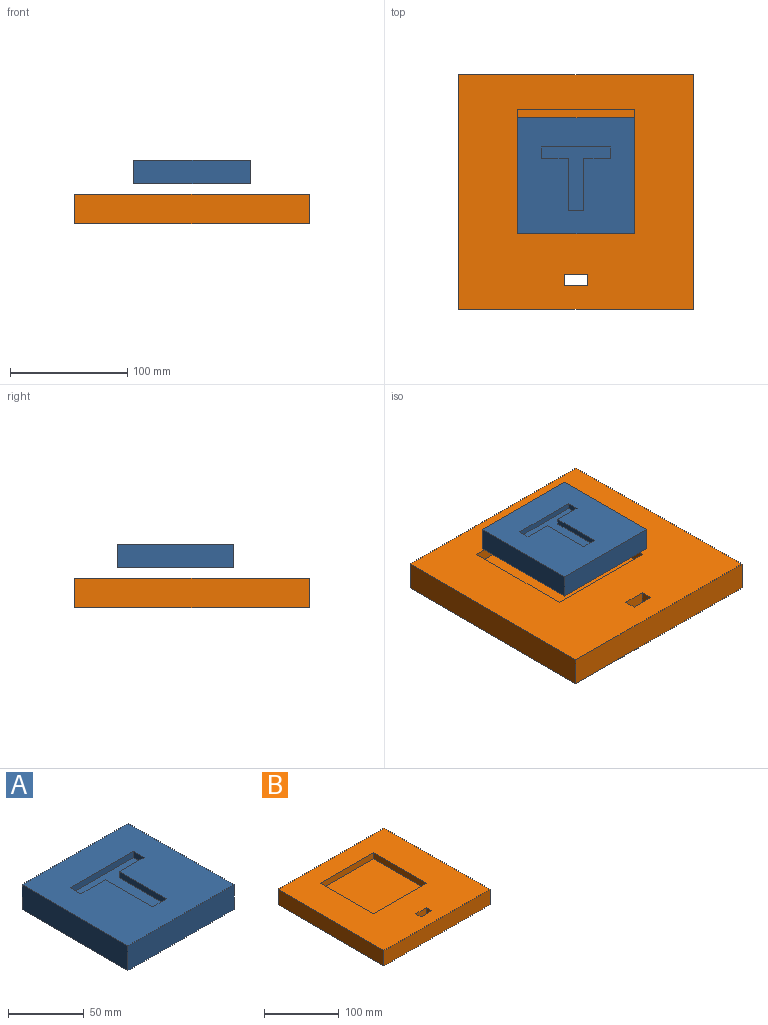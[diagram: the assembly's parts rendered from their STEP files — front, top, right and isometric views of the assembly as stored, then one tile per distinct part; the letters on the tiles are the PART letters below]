
ASSEMBLY  parts=2 mates=1
PART A: 15 faces, bbox 99x99x20 mm
  f0: plane 99x99mm, normal (0,0,1), area 8639mm2, adj f1,f2,f3,f4,f6,f7,f8,f9
  f1: plane 99x20mm, normal (0,-1,0), area 1980mm2, adj f0,f2,f4,f5
  f2: plane 99x20mm, normal (1,0,0), area 1980mm2, adj f0,f1,f3,f5
  f3: plane 99x20mm, normal (0,1,0), area 1980mm2, adj f0,f2,f4,f5
  f4: plane 99x20mm, normal (-1,0,0), area 1980mm2, adj f0,f1,f3,f5
  f5: plane 99x99mm, normal (0,0,-1), area 9801mm2, adj f1,f2,f3,f4
  f6: plane 59x5mm, normal (0,-1,0), area 295mm2, adj f0,f7,f13,f14
  f7: plane 10x5mm, normal (1,0,0), area 50mm2, adj f0,f6,f8,f14
  f8: plane 23x5mm, normal (0,1,0), area 115mm2, adj f0,f7,f9,f14
  f9: plane 44x5mm, normal (1,0,0), area 220mm2, adj f0,f8,f10,f14
  f10: plane 13x5mm, normal (0,1,0), area 65mm2, adj f0,f9,f11,f14
  f11: plane 44x5mm, normal (-1,0,0), area 220mm2, adj f0,f10,f12,f14
  f12: plane 23x5mm, normal (0,1,0), area 115mm2, adj f0,f11,f13,f14
  f13: plane 10x5mm, normal (-1,0,0), area 50mm2, adj f0,f6,f12,f14
  f14: plane 59x54mm, normal (0,0,1), area 1162mm2, adj f6,f7,f8,f9,f10,f11,f12,f13
PART B: 15 faces, bbox 200x200x25 mm
  f0: plane 200x200mm, normal (0,0,1), area 29800mm2, adj f2,f3,f4,f5,f6,f7,f8,f9
  f1: plane 200x200mm, normal (0,0,-1), area 39800mm2, adj f2,f3,f4,f5,f11,f12,f13,f14
  f2: plane 200x25mm, normal (0,1,0), area 5000mm2, adj f0,f1,f3,f5
  f3: plane 200x25mm, normal (-1,0,0), area 5000mm2, adj f0,f1,f2,f4
  f4: plane 200x25mm, normal (0,-1,0), area 5000mm2, adj f0,f1,f3,f5
  f5: plane 200x25mm, normal (1,0,0), area 5000mm2, adj f0,f1,f2,f4
  f6: plane 100x10mm, normal (0,-1,0), area 1000mm2, adj f0,f7,f9,f10
  f7: plane 100x10mm, normal (1,0,0), area 1000mm2, adj f0,f6,f8,f10
  f8: plane 100x10mm, normal (0,1,0), area 1000mm2, adj f0,f7,f9,f10
  f9: plane 100x10mm, normal (-1,0,0), area 1000mm2, adj f0,f6,f8,f10
  f10: plane 100x100mm, normal (0,0,1), area 10000mm2, adj f6,f7,f8,f9
  f11: plane 25x20mm, normal (0,-1,0), area 500mm2, adj f0,f1,f12,f14
  f12: plane 25x10mm, normal (1,0,0), area 250mm2, adj f0,f1,f11,f13
  f13: plane 25x20mm, normal (0,1,0), area 500mm2, adj f0,f1,f12,f14
  f14: plane 25x10mm, normal (-1,0,0), area 250mm2, adj f0,f1,f11,f13
PLACE A t=(-50.5,64.29,34.15)mm
PLACE B at identity fixed
MATE slider B.f10 <-> A.f14  axis (0,0,1) through (-100,120,15)mm
